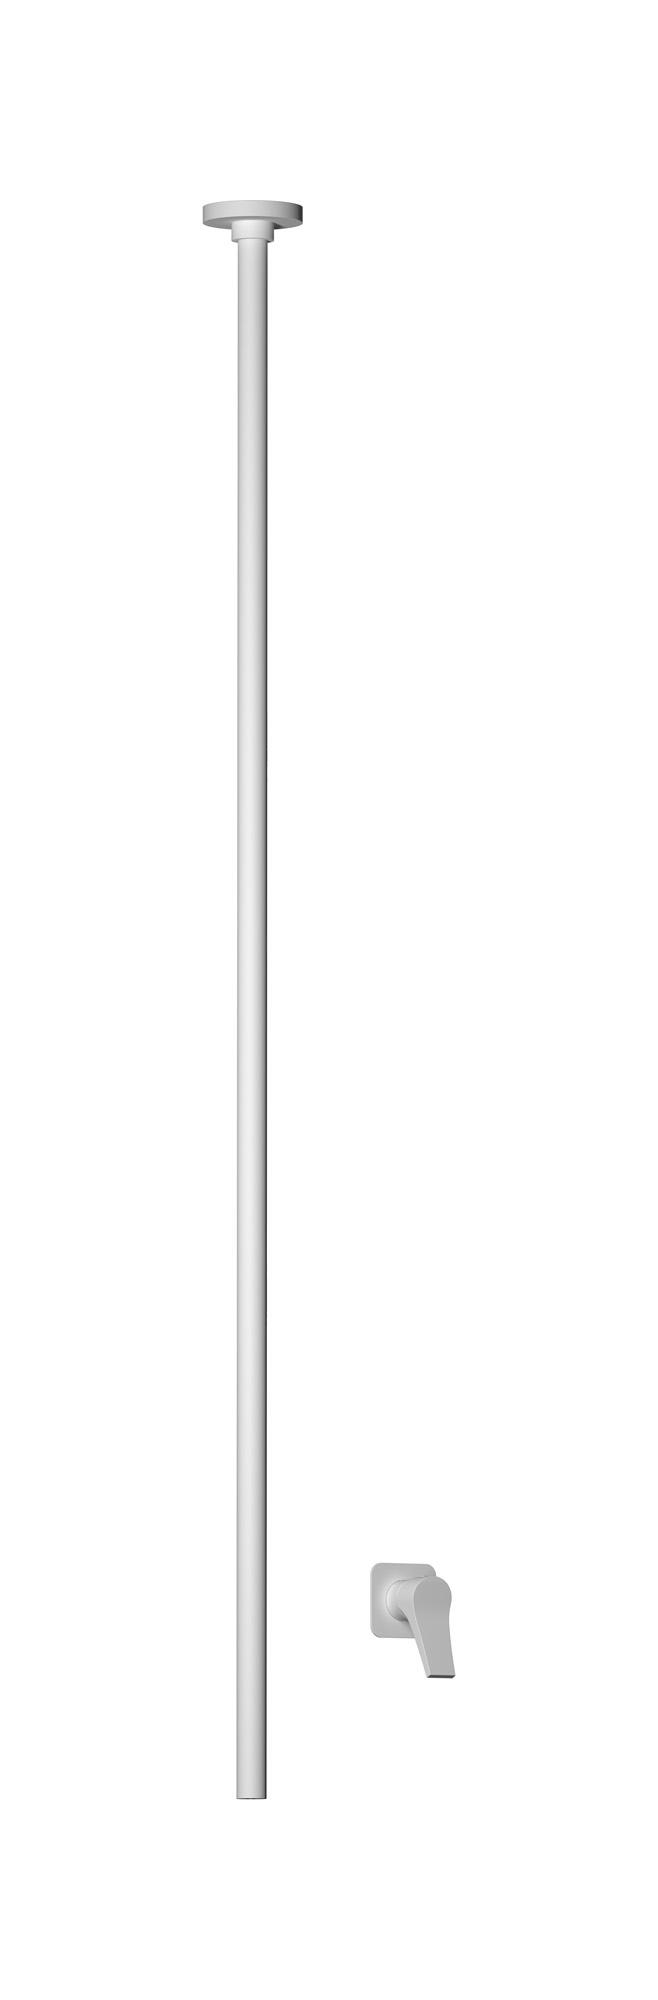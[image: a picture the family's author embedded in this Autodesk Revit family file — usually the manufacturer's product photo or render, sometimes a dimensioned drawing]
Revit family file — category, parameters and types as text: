
# Revit family: TW210
name_source: partatom
category: Apparecchi idraulici
units: mm (PartAtom-declared; Revit-internal decimal feet)

## family parameters
Basato su piano di lavoro = No
Condiviso = No
Mantieni orientamento annotazione = No
Numero OmniClass = 23.45.55.17
Punto di calcolo locali = No
Quota connettore circolare = Usa diametro
Sempre verticale = Sì
Taglio con vuoti quando caricato = No
Tipo di parte = Normale
Titolo OmniClass = Mixing Faucets

## types (4) — shared parameters
Cold water inlet = 10 mm  [stored 0.0328084 ft]
Commenti sul tipo = Wall mixer
Connessione CW = No
Connessione HW = No
Connessione di scarico = No
Connessione di ventilazione = No
Descrizione = Ceiling spout with wall mounted mixer
Hot water inlet = 10 mm  [stored 0.0328084 ft]
Produttore = IB Rubinetterie S.p.A.
URL = https://www.weareib.it
zero-valued in all types: Prospetto di default

## per-type parameters (varying)
| type | Finishes surface | Immagine tipo | Modello |
| Chrome | IB_Chrome | TW210CC copia.jpg | TW210CC |
| Brushed nickel | IB_Brushed nickel | TW210SS copia.jpg | TW210SS |
| Matt white | IB_matt white | TW210BO copia.jpg | TW210BO |
| Matt black | IB_matt black | TW210NP copia.jpg | TW210NP |

note: [stored X ft] marks values corroborated as IEEE doubles in the binary element streams (Revit-internal decimal feet)
